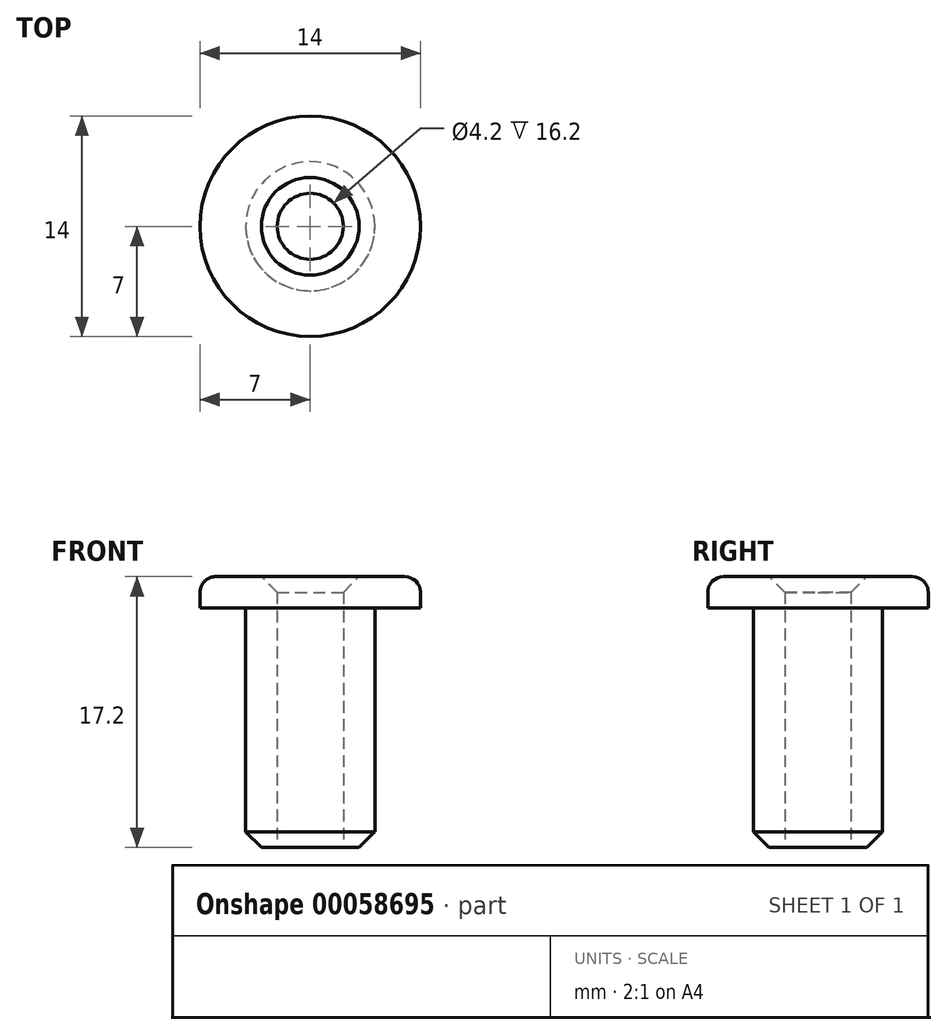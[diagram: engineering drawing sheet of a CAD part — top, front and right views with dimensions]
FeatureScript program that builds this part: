
annotation { "Feature Type Name" : "Feature", "Feature Type Description" : "" }
export const myFeature = defineFeature(function(context is Context, id is Id, definition is map)
    precondition{}
    {
        {
            var Q0;
            Q0=qCreatedBy(makeId("Front.planeOp"),FACE);
            var sketch = newSketch(context, id + "F0", { "sketchPlane" : qUnion([Q0])});
            skLineSegment(sketch, "E0", {"start": v(0, 0) * mm, "end": v(0, 17.2) * mm, "construction": true});
            skLineSegment(sketch, "E1", {"start": v(2.1, 17.2) * mm, "end": v(7, 17.2) * mm});
            skLineSegment(sketch, "E2", {"start": v(7, 17.2) * mm, "end": v(7, 15.2) * mm});
            skLineSegment(sketch, "E3", {"start": v(7, 15.2) * mm, "end": v(4.1, 15.2) * mm});
            skLineSegment(sketch, "E4", {"start": v(4.1, 15.2) * mm, "end": v(4.1, 0) * mm});
            skLineSegment(sketch, "E5", {"start": v(4.1, 0) * mm, "end": v(2.1, 0) * mm});
            skLineSegment(sketch, "E6", {"start": v(2.1, 0) * mm, "end": v(2.1, 17.2) * mm});
            skSolve(sketch);
        }
        {
            var Q0;
            Q0 = qSketchRegion(id + "F0", true);
            var Q1;
            Q1=sQuery(id+"F0.wireOp",EDGE,"E0");
            revolve(context, id + "F1", {"entities" : qUnion([Q0]), "axis" : qUnion([Q1]), "revolveType" : RevolveType.FULL});
        }
        {
            var Q0;
            Q0=makeQuery(id+"F1.opRevolve","SWEPT_EDGE",EDGE,{"disambiguationData":[OSD([sQuery(id+"F0.wireOp",EDGE,"E1"),sQuery(id+"F0.wireOp",EDGE,"E6")])]});
            var Q1;
            Q1=makeQuery(id+"F1.opRevolve","SWEPT_EDGE",EDGE,{"disambiguationData":[OSD([sQuery(id+"F0.wireOp",EDGE,"E4"),sQuery(id+"F0.wireOp",EDGE,"E5")])]});
            chamfer(context, id + "F2", {"entities" : qUnion([Q0, Q1]), "width" : 1 * mm, "tangentPropagation" : true});
        }
        {
            var Q0;
            Q0=makeQuery(id+"F1.opRevolve","SWEPT_EDGE",EDGE,{"disambiguationData":[OSD([sQuery(id+"F0.wireOp",EDGE,"E1"),sQuery(id+"F0.wireOp",EDGE,"E2")])]});
            fillet(context, id + "F3", {"entities" : qUnion([Q0]), "radius" : 1 * mm, "tangentPropagation" : true, "allowEdgeOverflow" : false});
        }
    });
